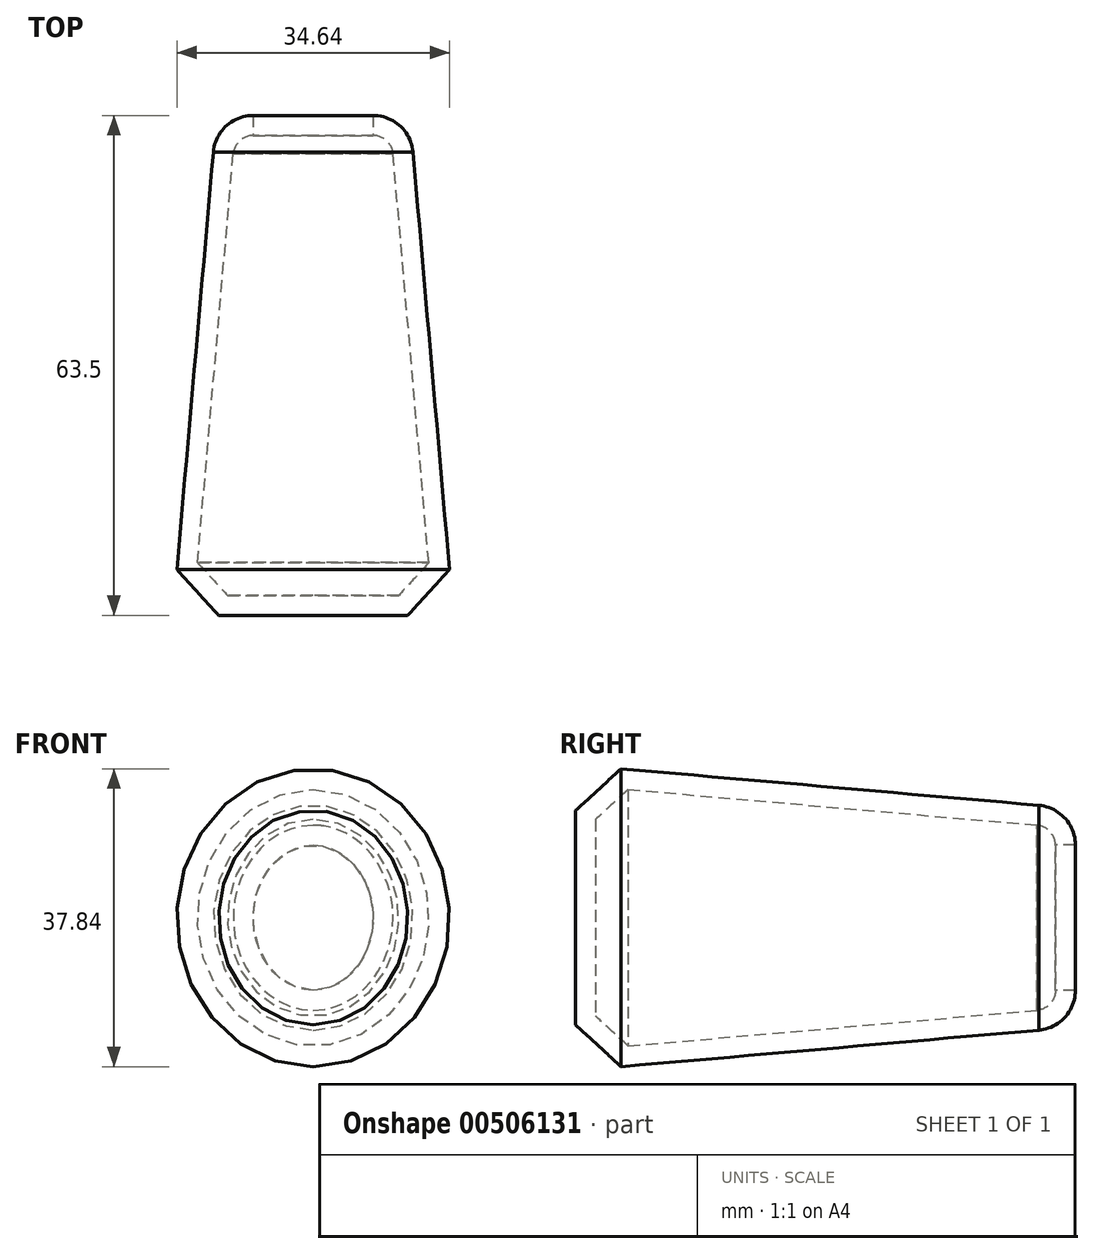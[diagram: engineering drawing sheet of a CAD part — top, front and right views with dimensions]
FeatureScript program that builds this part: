
annotation { "Feature Type Name" : "Feature", "Feature Type Description" : "" }
export const myFeature = defineFeature(function(context is Context, id is Id, definition is map)
    precondition{}
    {
        {
            var Q0;
            Q0=qCreatedBy(makeId("Front.planeOp"),FACE);
            var sketch = newSketch(context, id + "F0", { "sketchPlane" : qUnion([Q0])});
            skEllipse(sketch, "E0", {"center": v(0, 0) * mm, "majorRadius": 13.88 * mm, "minorRadius": 12.27 * mm, "majorAxis": v(0, 1)});
            skSolve(sketch);
        }
        {
            var Q0;
            Q0 = qSketchRegion(id + "F0", true);
            extrude(context, id + "F1", {"entities" : qUnion([Q0]), "depth" : 63.5 * mm, "hasDraft" : true, "draftAngle" : 5 * degree});
        }
        {
            var Q0;
            Q0=makeQuery(id+"F1.opExtrude","CAP_FACE",FACE,{"disambiguationData":[OSD([sQuery(id+"F0.wireOp",EDGE,"E0")])],"isStart":false});
            chamfer(context, id + "F2", {"entities" : qUnion([Q0]), "width" : 5.33 * mm, "tangentPropagation" : true});
        }
        {
            var Q0;
            Q0=makeQuery(id+"F1.opExtrude","CAP_FACE",FACE,{"disambiguationData":[OSD([sQuery(id+"F0.wireOp",EDGE,"E0")])],"isStart":true});
            fillet(context, id + "F3", {"entities" : qUnion([Q0]), "radius" : 5.08 * mm, "tangentPropagation" : true, "allowEdgeOverflow" : false});
        }
        {
            var Q0;
            Q0=makeQuery(id+"F1.opExtrude","CAP_FACE",FACE,{"disambiguationData":[OSD([sQuery(id+"F0.wireOp",EDGE,"E0")])],"isStart":true});
            shell(context, id + "F4", {"entities" : qUnion([Q0]), "thickness" : 2.54 * mm});
        }
    });
